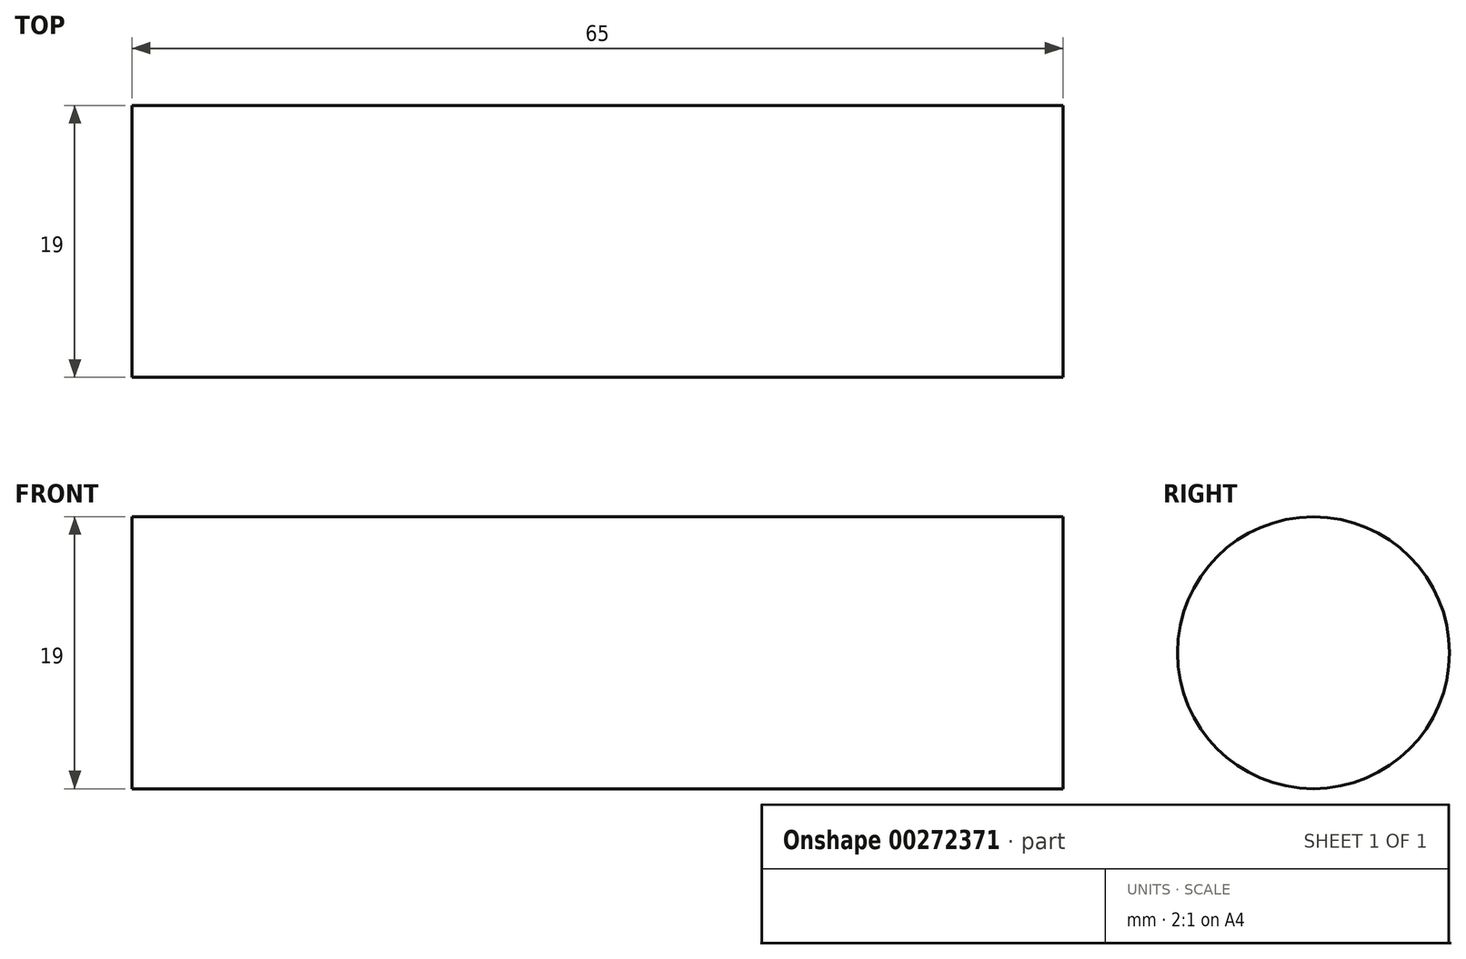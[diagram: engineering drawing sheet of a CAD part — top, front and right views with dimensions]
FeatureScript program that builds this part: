
annotation { "Feature Type Name" : "Feature", "Feature Type Description" : "" }
export const myFeature = defineFeature(function(context is Context, id is Id, definition is map)
    precondition{}
    {
        {
            var Q0;
            Q0=qCreatedBy(makeId("Right.planeOp"),FACE);
            var sketch = newSketch(context, id + "F0", { "sketchPlane" : qUnion([Q0])});
            skCircle(sketch, "E0", {"center": v(0, 0) * mm, "radius": 9.5 * mm});
            skSolve(sketch);
        }
        {
            var Q0;
            Q0=makeQuery(id+"F0.imprint","IMPRINT",FACE,{"disambiguationData":[TD([[makeQuery(id+"F0.imprint","IMPRINT",EDGE,{"derivedFrom":sQuery(id+"F0.wireOp",EDGE,"E0")}),1.0]])]});
            extrude(context, id + "F1", {"entities" : qUnion([Q0]), "depth" : 65 * mm});
        }
    });
